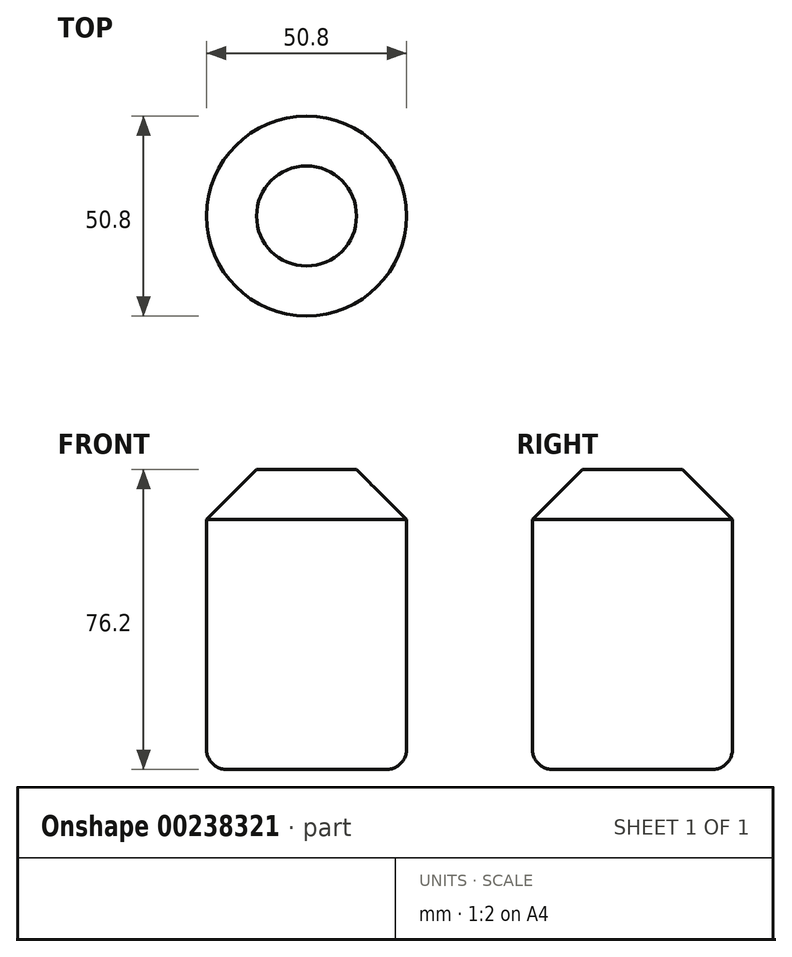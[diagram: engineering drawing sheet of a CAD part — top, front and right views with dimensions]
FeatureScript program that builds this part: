
annotation { "Feature Type Name" : "Feature", "Feature Type Description" : "" }
export const myFeature = defineFeature(function(context is Context, id is Id, definition is map)
    precondition{}
    {
        {
            var Q0;
            Q0=qCreatedBy(makeId("Top.planeOp"),FACE);
            var sketch = newSketch(context, id + "F0", { "sketchPlane" : qUnion([Q0])});
            skCircle(sketch, "E0", {"center": v(0, 0) * mm, "radius": 25.4 * mm});
            skSolve(sketch);
        }
        {
            var Q0;
            Q0=makeQuery(id+"F0.imprint","IMPRINT",FACE,{"disambiguationData":[TD([[makeQuery(id+"F0.imprint","IMPRINT",EDGE,{"derivedFrom":sQuery(id+"F0.wireOp",EDGE,"E0")}),1.0]])]});
            extrude(context, id + "F1", {"entities" : qUnion([Q0]), "depth" : 76.2 * mm});
        }
        {
            var Q0;
            Q0=makeQuery(id+"F1.opExtrude","CAP_FACE",FACE,{"disambiguationData":[OSD([sQuery(id+"F0.wireOp",EDGE,"E0")])],"isStart":false});
            chamfer(context, id + "F2", {"entities" : qUnion([Q0]), "width" : 12.7 * mm, "tangentPropagation" : true});
        }
        {
            var Q0;
            Q0=makeQuery(id+"F1.opExtrude","CAP_FACE",FACE,{"disambiguationData":[OSD([sQuery(id+"F0.wireOp",EDGE,"E0")])],"isStart":true});
            fillet(context, id + "F3", {"entities" : qUnion([Q0]), "radius" : 5.08 * mm, "tangentPropagation" : true, "allowEdgeOverflow" : false});
        }
    });
